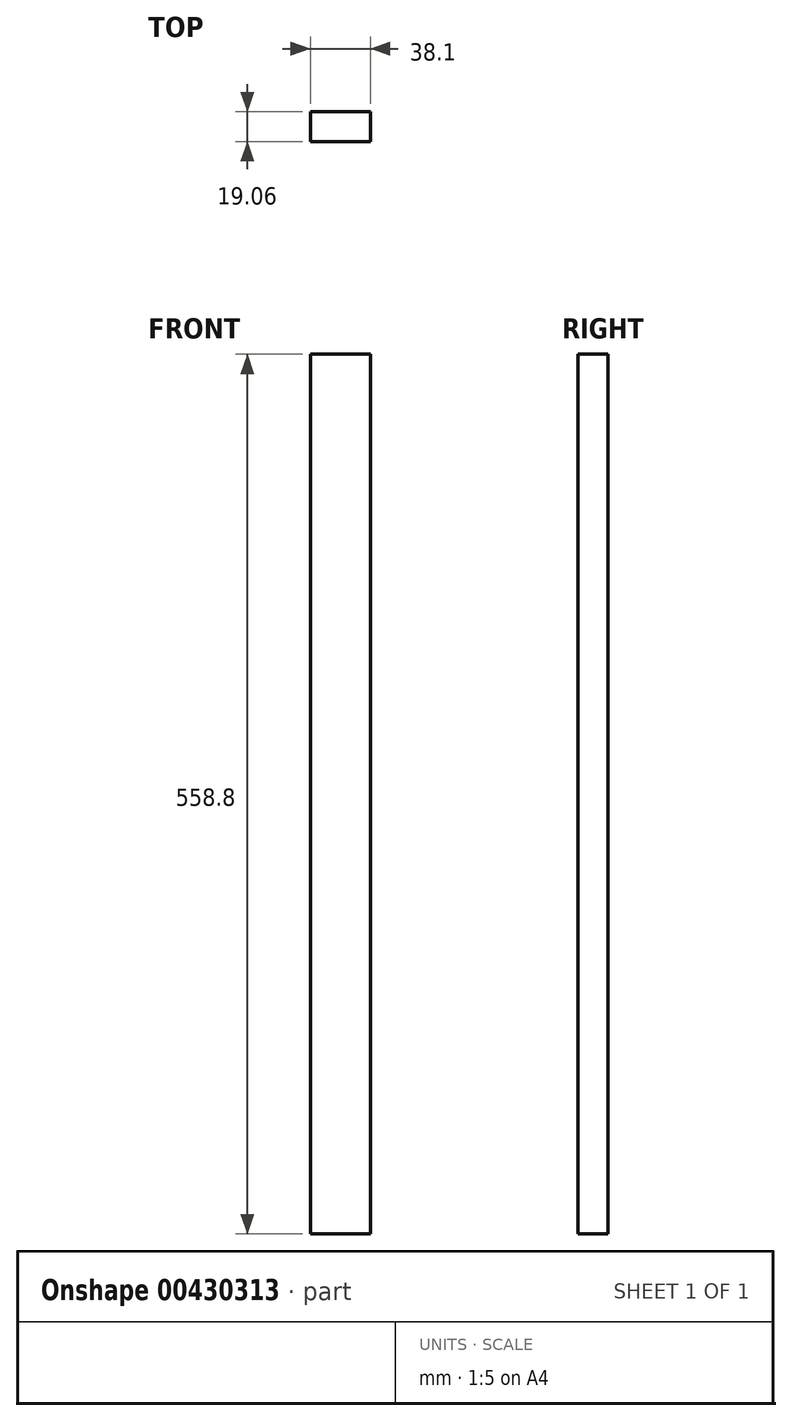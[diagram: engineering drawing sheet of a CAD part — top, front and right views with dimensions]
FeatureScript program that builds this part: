
annotation { "Feature Type Name" : "Feature", "Feature Type Description" : "" }
export const myFeature = defineFeature(function(context is Context, id is Id, definition is map)
    precondition{}
    {
        {
            var Q0;
            Q0=qCreatedBy(makeId("Top.planeOp"),FACE);
            var sketch = newSketch(context, id + "F0", { "sketchPlane" : qUnion([Q0])});
            skLineSegment(sketch, "E0.bottom", {"start": v(19.05, 9.53) * mm, "end": v(-19.05, 9.53) * mm});
            skLineSegment(sketch, "E0.top", {"start": v(19.05, -9.53) * mm, "end": v(-19.05, -9.53) * mm});
            skLineSegment(sketch, "E0.left", {"start": v(19.05, 9.53) * mm, "end": v(19.05, -9.53) * mm});
            skLineSegment(sketch, "E0.right", {"start": v(-19.05, 9.53) * mm, "end": v(-19.05, -9.53) * mm});
            skPoint(sketch, "E0.middle", {"position": v(0, 0) * mm});
            skSolve(sketch);
        }
        {
            var Q0;
            Q0=qSketchRegion(id+"F0",true);
            extrude(context, id + "F1", {"entities" : qUnion([Q0]), "depth" : 558.8 * mm});
        }
    });
